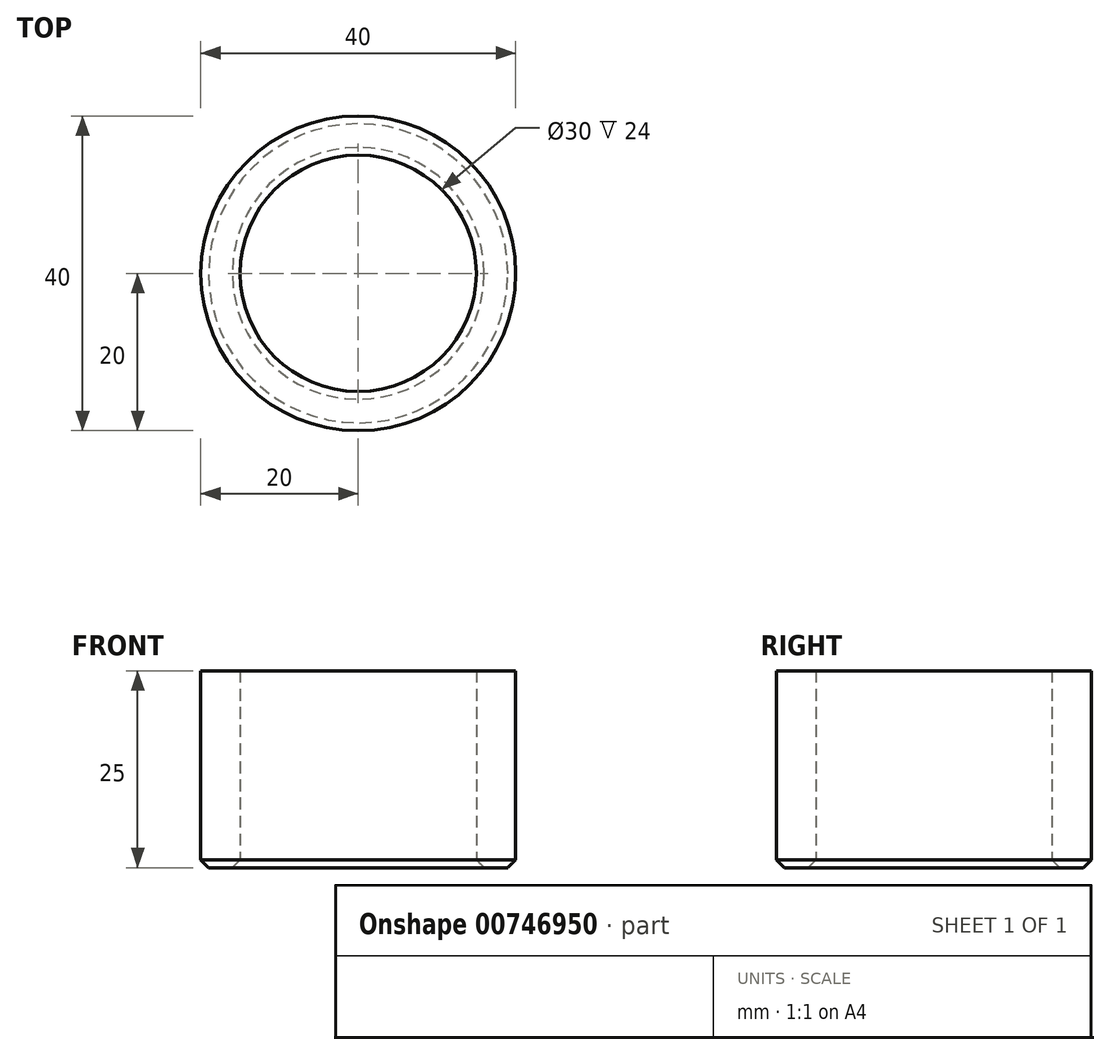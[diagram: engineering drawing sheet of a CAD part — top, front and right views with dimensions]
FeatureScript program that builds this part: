
annotation { "Feature Type Name" : "Feature", "Feature Type Description" : "" }
export const myFeature = defineFeature(function(context is Context, id is Id, definition is map)
    precondition{}
    {
        {
            var Q0;
            Q0=qCreatedBy(makeId("Top.planeOp"),FACE);
            var sketch = newSketch(context, id + "F0", { "sketchPlane" : qUnion([Q0])});
            skCircle(sketch, "E0", {"center": v(0, 0) * mm, "radius": 20 * mm});
            skCircle(sketch, "E1.0", {"center": v(0, 0) * mm, "radius": 15 * mm});
            skSolve(sketch);
        }
        {
            var Q0;
            Q0=makeQuery(id+"F0.imprint","IMPRINT",FACE,{"disambiguationData":[TD([[makeQuery(id+"F0.imprint","IMPRINT",EDGE,{"derivedFrom":sQuery(id+"F0.wireOp",EDGE,"E0")}),1.0]])]});
            extrude(context, id + "F1", {"entities" : qUnion([Q0]), "depth" : 25 * mm, "offsetDistance" : 25 * mm});
        }
        {
            var Q0;
            Q0=makeQuery(id+"F1.opExtrude","CAP_EDGE",EDGE,{"disambiguationData":[OSD([sQuery(id+"F0.wireOp",EDGE,"E0")])],"isStart":true});
            var Q1;
            Q1=makeQuery(id+"F1.opExtrude","CAP_EDGE",EDGE,{"disambiguationData":[OSD([sQuery(id+"F0.wireOp",EDGE,"E1.0")])],"isStart":true});
            chamfer(context, id + "F2", {"entities" : qUnion([Q0, Q1]), "width" : 1 * mm, "tangentPropagation" : true});
        }
    });
